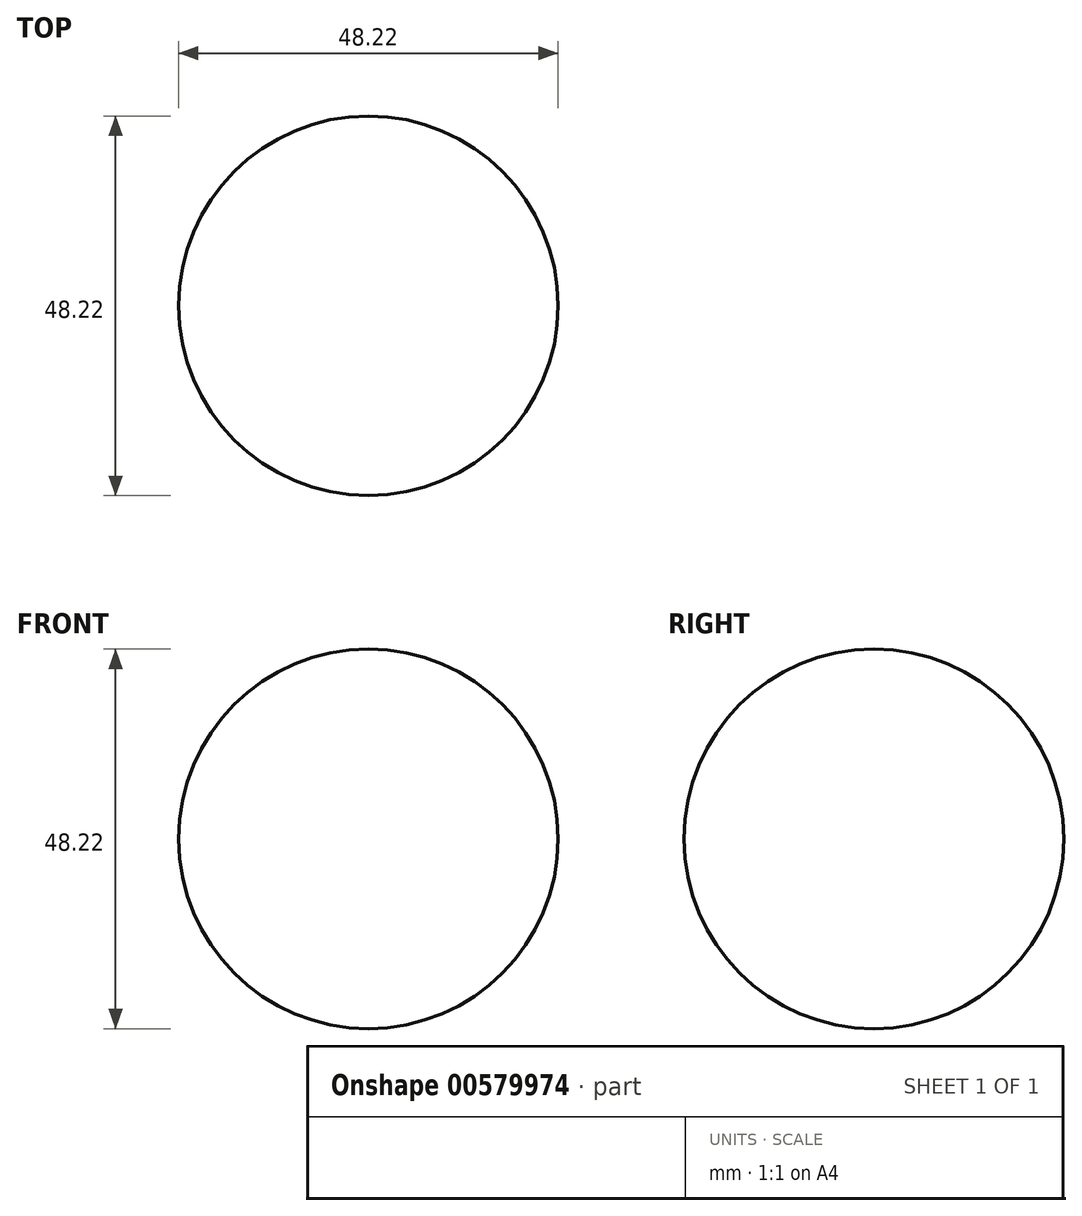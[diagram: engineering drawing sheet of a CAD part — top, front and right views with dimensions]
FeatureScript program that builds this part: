
annotation { "Feature Type Name" : "Feature", "Feature Type Description" : "" }
export const myFeature = defineFeature(function(context is Context, id is Id, definition is map)
    precondition{}
    {
        {
            var Q0;
            Q0=qCreatedBy(makeId("Front.planeOp"),FACE);
            var sketch = newSketch(context, id + "F0", { "sketchPlane" : qUnion([Q0])});
            skArc(sketch, "E0", {"start": v(0, 24.1) * mm, "mid": v(-24.1, 0) * mm, "end": v(0, -24.1) * mm});
            skLineSegment(sketch, "E1", {"start": v(0, 24.1) * mm, "end": v(0, -24.1) * mm});
            skSolve(sketch);
        }
        {
            var Q0;
            Q0=makeQuery(id+"F0.imprint","IMPRINT",FACE,{"disambiguationData":[TD([[makeQuery(id+"F0.imprint","IMPRINT",EDGE,{"derivedFrom":sQuery(id+"F0.wireOp",EDGE,"E0")}),1.0]])]});
            var Q1;
            Q1=sQuery(id+"F0.wireOp",EDGE,"E1");
            revolve(context, id + "F1", {"entities" : qUnion([Q0]), "axis" : qUnion([Q1]), "revolveType" : RevolveType.FULL});
        }
    });
